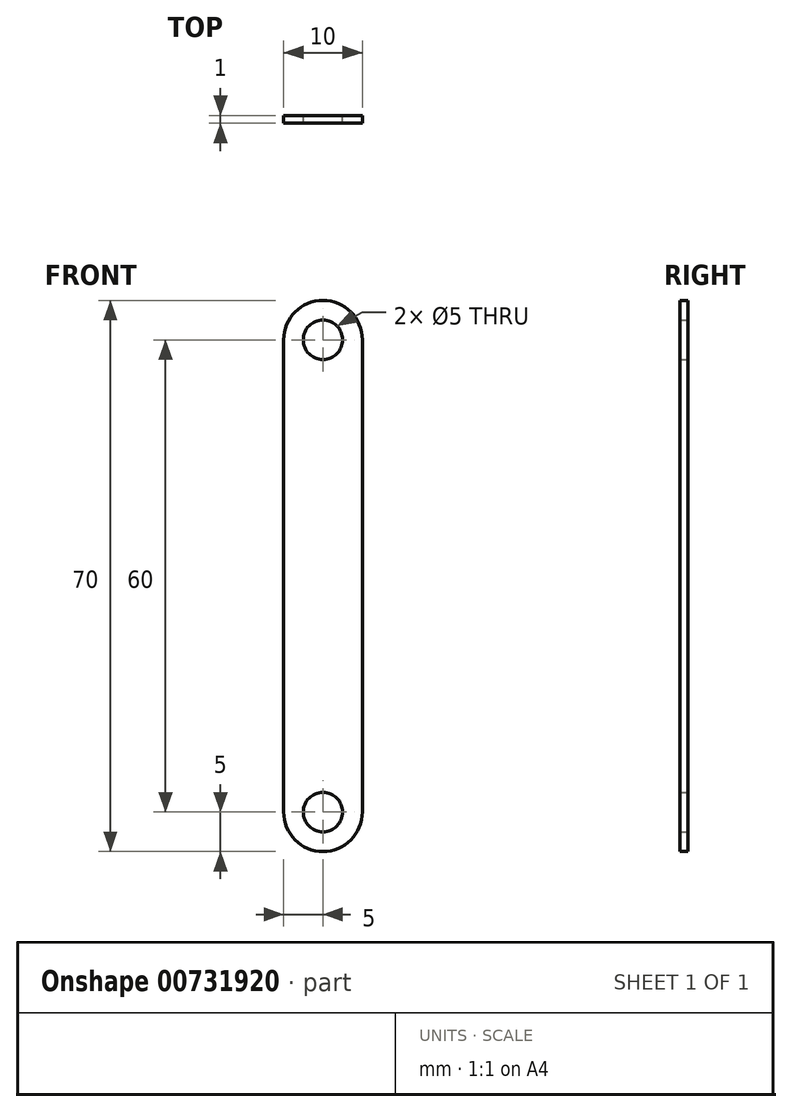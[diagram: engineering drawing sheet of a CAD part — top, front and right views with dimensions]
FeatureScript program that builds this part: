
annotation { "Feature Type Name" : "Feature", "Feature Type Description" : "" }
export const myFeature = defineFeature(function(context is Context, id is Id, definition is map)
    precondition{}
    {
        {
            var Q0;
            Q0=qCreatedBy(makeId("Front.planeOp"),FACE);
            var sketch = newSketch(context, id + "F0", { "sketchPlane" : qUnion([Q0])});
            skArc(sketch, "E0", {"start": v(5, 30) * mm, "mid": v(0, 35) * mm, "end": v(-5, 30) * mm});
            skArc(sketch, "E1", {"start": v(-5, -30) * mm, "mid": v(0, -35) * mm, "end": v(5, -30) * mm});
            skCircle(sketch, "E2", {"center": v(0, -30) * mm, "radius": 2.5 * mm});
            skCircle(sketch, "E3", {"center": v(0, 30) * mm, "radius": 2.5 * mm});
            skLineSegment(sketch, "E4", {"start": v(5, 30) * mm, "end": v(5, -30) * mm});
            skLineSegment(sketch, "E5", {"start": v(-5, -30) * mm, "end": v(-5, 30) * mm});
            skSolve(sketch);
        }
        {
            var Q0;
            Q0=qSketchRegion(id+"F0",true);
            extrude(context, id + "F1", {"entities" : qUnion([Q0]), "depth" : 1 * mm, "offsetDistance" : 25.4 * mm});
        }
    });
